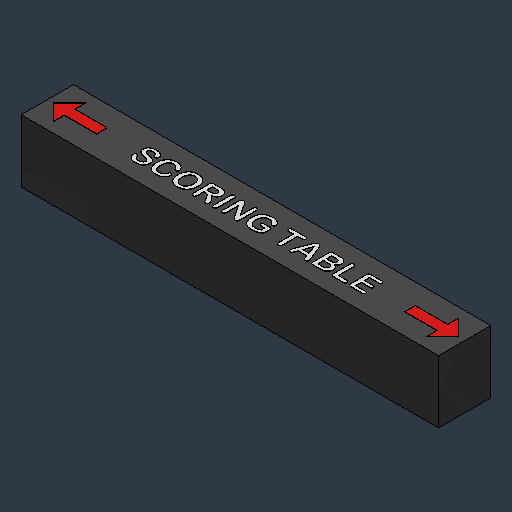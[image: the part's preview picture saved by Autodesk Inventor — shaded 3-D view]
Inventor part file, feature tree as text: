
AUTODESK INVENTOR PART (.ipt)
format: ipt  version: 2024.3 (Build 283343000, 343)  size: 580,096 bytes
history: native  units: mm (DEFAULTED — no unit token found)
features: other x14, mirror x1
ambient origin geometry x8: Origin, YZ Plane, XZ Plane, XY Plane, X Axis, Y Axis, Z Axis, Center Point
bodies: Solid1 (feature_tree), Solid2 (feature_tree), Solid3 (feature_tree), Solid4 (feature_tree), Solid5 (feature_tree), Solid6 (feature_tree), Solid7 (feature_tree), Solid8 (feature_tree), Solid9 (feature_tree), Solid10 (feature_tree), Solid11 (feature_tree), Solid12 (feature_tree), Solid13 (feature_tree), Solid14 (feature_tree), Solid15 (feature_tree)
feature tree (15):
  other  "Boss-Extrude1"
  other  "Boss-Extrude2[1]"
  other  "Boss-Extrude2[2]"
  other  "Boss-Extrude2[3]"
  other  "Boss-Extrude2[4]"
  other  "Boss-Extrude2[5]"
  other  "Boss-Extrude2[6]"
  other  "Boss-Extrude2[7]"
  other  "Boss-Extrude2[8]"
  other  "Boss-Extrude2[9]"
  other  "Boss-Extrude2[10]"
  other  "Boss-Extrude2[11]"
  other  "Boss-Extrude2[12]"
  other  "Boss-Extrude3"
  mirror  "Mirror1"
